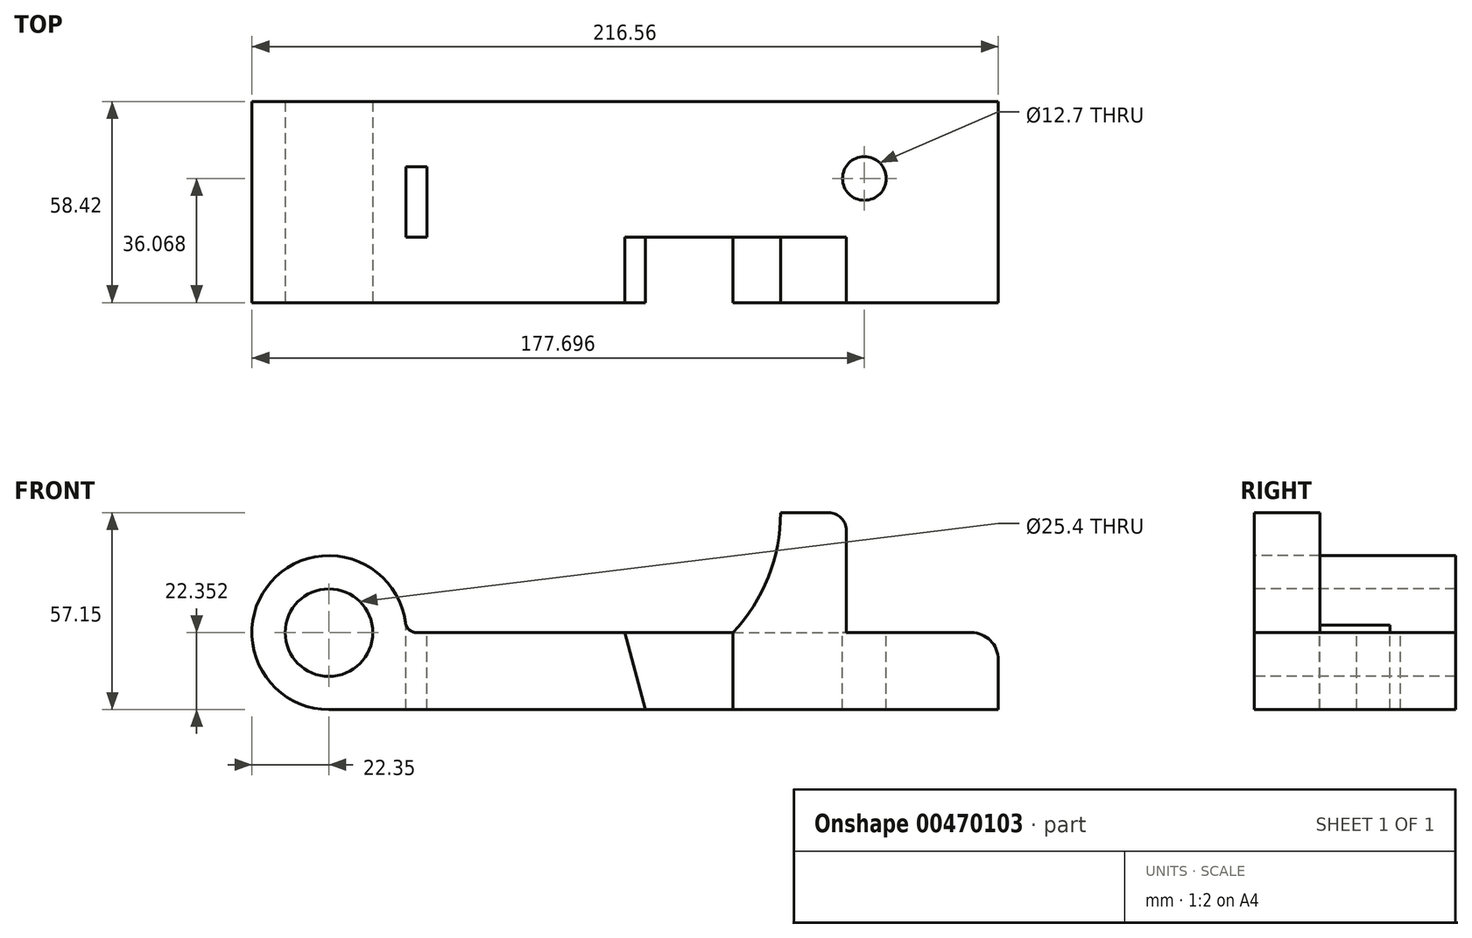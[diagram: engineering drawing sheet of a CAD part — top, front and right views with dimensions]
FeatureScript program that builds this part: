
annotation { "Feature Type Name" : "Feature", "Feature Type Description" : "" }
export const myFeature = defineFeature(function(context is Context, id is Id, definition is map)
    precondition{}
    {
        {
            var Q0;
            Q0=qCreatedBy(makeId("Front.planeOp"),FACE);
            var sketch = newSketch(context, id + "F0", { "sketchPlane" : qUnion([Q0])});
            skLineSegment(sketch, "E0", {"start": v(0, 0) * mm, "end": v(194.2, 0) * mm});
            skCircle(sketch, "E1", {"center": v(0, 22.35) * mm, "radius": 22.35 * mm});
            skPoint(sketch, "E1.second.point", {"position": v(-2.3, 44.58) * mm});
            skPoint(sketch, "E1.third.point", {"position": v(17.77, 35.9) * mm});
            skCircle(sketch, "E2", {"center": v(0, 22.35) * mm, "radius": 12.7 * mm});
            skLineSegment(sketch, "E3", {"start": v(22.35, 22.35) * mm, "end": v(194.2, 22.35) * mm});
            skLineSegment(sketch, "E4", {"start": v(194.2, 22.35) * mm, "end": v(194.2, 0) * mm});
            skLineSegment(sketch, "E5", {"start": v(91.85, 0) * mm, "end": v(85.85, 22.35) * mm});
            skLineSegment(sketch, "E6", {"start": v(117.25, 22.35) * mm, "end": v(117.25, 0) * mm});
            skLineSegment(sketch, "E7", {"start": v(131.04, 57.15) * mm, "end": v(150.09, 57.15) * mm});
            skLineSegment(sketch, "E8", {"start": v(150.09, 57.15) * mm, "end": v(150.09, 22.35) * mm});
            skArc(sketch, "E9", {"start": v(117.25, 22.35) * mm, "mid": v(127.46, 38.43) * mm, "end": v(131.04, 57.15) * mm});
            skPoint(sketch, "E9.third.point", {"position": v(126.77, 36.77) * mm});
            skSolve(sketch);
        }
        {
            var Q0;
            {var subQ0=sQuery(id+"F0.wireOp",EDGE,"E5");Q0=makeQuery(id+"F0.imprint","IMPRINT",FACE,{"disambiguationData":[TD([[makeQuery(id+"F0.imprint","IMPRINT",EDGE,{"derivedFrom":subQ0}),-1.0]])]});}
            var Q1;
            {var subQ3=sQuery(id+"F0.wireOp",EDGE,"E5");Q1=makeQuery(id+"F0.imprint","IMPRINT",FACE,{"disambiguationData":[TD([[makeQuery(id+"F0.imprint","IMPRINT",EDGE,{"derivedFrom":subQ3}),1.0]])]});}
            var Q2;
            {var subQ0=sQuery(id+"F0.wireOp",EDGE,"E4");Q2=makeQuery(id+"F0.imprint","IMPRINT",FACE,{"disambiguationData":[TD([[makeQuery(id+"F0.imprint","IMPRINT",EDGE,{"derivedFrom":subQ0}),-1.0]])]});}
            var Q3;
            Q3=makeQuery(id+"F0.imprint","IMPRINT",FACE,{"disambiguationData":[TD([[makeQuery(id+"F0.imprint","IMPRINT",EDGE,{"derivedFrom":sQuery(id+"F0.wireOp",EDGE,"E2")}),-1.0]])]});
            extrude(context, id + "F1", {"entities" : qUnion([Q0, Q1, Q2, Q3]), "oppositeDirection" : true, "depth" : 58.42 * mm});
        }
        {
            var Q0;
            {var subQ0=sQuery(id+"F0.wireOp",EDGE,"E5");Q0=makeQuery(id+"F0.imprint","IMPRINT",FACE,{"disambiguationData":[TD([[makeQuery(id+"F0.imprint","IMPRINT",EDGE,{"derivedFrom":subQ0}),-1.0]])]});}
            extrude(context, id + "F2", {"entities" : qUnion([Q0]), "operationType" : NewBodyOperationType.REMOVE, "oppositeDirection" : true, "depth" : 19.05 * mm});
        }
        {
            var Q0;
            Q0=makeQuery(id+"F0.imprint","IMPRINT",FACE,{"disambiguationData":[TD([[makeQuery(id+"F0.imprint","IMPRINT",EDGE,{"derivedFrom":sQuery(id+"F0.wireOp",EDGE,"E7")}),-1.0]])]});
            extrude(context, id + "F3", {"entities" : qUnion([Q0]), "operationType" : NewBodyOperationType.ADD, "oppositeDirection" : true, "depth" : 19.05 * mm});
        }
        {
            var Q0;
            Q0=makeQuery(id+"F1.opExtrude","SWEPT_FACE",FACE,{"disambiguationData":[OSD([sQuery(id+"F0.wireOp",EDGE,"E3")])]});
            var sketch = newSketch(context, id + "F4", { "sketchPlane" : qUnion([Q0])});
            skCircle(sketch, "E10", {"center": v(155.35, 36.07) * mm, "radius": 6.35 * mm});
            skLineSegment(sketch, "E11.bottom", {"start": v(-22.35, 19) * mm, "end": v(28.45, 19) * mm});
            skLineSegment(sketch, "E11.top", {"start": v(-22.35, 39.42) * mm, "end": v(28.45, 39.42) * mm});
            skLineSegment(sketch, "E11.left", {"start": v(-22.35, 19) * mm, "end": v(-22.35, 39.42) * mm});
            skLineSegment(sketch, "E11.right", {"start": v(28.45, 19) * mm, "end": v(28.45, 39.42) * mm});
            skLineSegment(sketch, "E12", {"start": v(-22.35, 0) * mm, "end": v(-22.35, 58.42) * mm});
            skSolve(sketch);
        }
        {
            var Q0;
            Q0=makeQuery(id+"F4.imprint","IMPRINT",FACE,{"disambiguationData":[TD([[makeQuery(id+"F4.imprint","IMPRINT",EDGE,{"derivedFrom":sQuery(id+"F4.wireOp",EDGE,"2CULlB4I-Zh7y-c74u-416q-1Dsw6ONQlv81.bottom")}),1.0]])]});
            var Q1;
            Q1=makeQuery(id+"F4.imprint","IMPRINT",FACE,{"disambiguationData":[TD([[makeQuery(id+"F4.imprint","IMPRINT",EDGE,{"derivedFrom":sQuery(id+"F4.wireOp",EDGE,"E10")}),1.0]])]});
            extrude(context, id + "F5", {"entities" : qUnion([Q0, Q1]), "operationType" : NewBodyOperationType.REMOVE, "endBound" : BoundingType.SYMMETRIC, "oppositeDirection" : true, "depth" : 76.2 * mm});
        }
        {
            var Q0;
            Q0=makeQuery(id+"F1.opExtrude","SWEPT_EDGE",EDGE,{"disambiguationData":[OSD([sQuery(id+"F0.wireOp",EDGE,"E1"),sQuery(id+"F0.wireOp",EDGE,"E3")])]});
            var Q1;
            Q1=makeQuery(id+"F3.opExtrude","SWEPT_EDGE",EDGE,{"disambiguationData":[OSD([sQuery(id+"F0.wireOp",EDGE,"E3"),sQuery(id+"F0.wireOp",EDGE,"E8")])]});
            fillet(context, id + "F6", {"entities" : qUnion([Q0, Q1]), "radius" : 3.3 * mm, "tangentPropagation" : true, "allowEdgeOverflow" : false});
        }
        {
            var Q0;
            Q0=makeQuery(id+"F3.opExtrude","SWEPT_EDGE",EDGE,{"disambiguationData":[OSD([sQuery(id+"F0.wireOp",EDGE,"E7"),sQuery(id+"F0.wireOp",EDGE,"E8")])]});
            fillet(context, id + "F7", {"entities" : qUnion([Q0]), "radius" : 5.08 * mm, "tangentPropagation" : true, "allowEdgeOverflow" : false});
        }
        {
            var Q0;
            Q0=makeQuery(id+"F1.opExtrude","SWEPT_EDGE",EDGE,{"disambiguationData":[OSD([sQuery(id+"F0.wireOp",EDGE,"E3"),sQuery(id+"F0.wireOp",EDGE,"E4")])]});
            fillet(context, id + "F8", {"entities" : qUnion([Q0]), "radius" : 7.87 * mm, "tangentPropagation" : true, "allowEdgeOverflow" : false});
        }
        {
            var Q0;
            {var subQ0=sQuery(id+"F4.wireOp",EDGE,"E12");var subQ1=sQuery(id+"F4.wireOp",EDGE,"E11.bottom");var subQ2=makeQuery(id+"F4.imprint","INTERSECT",VERTEX,{"derivedFrom":[subQ1,subQ0]});Q0=makeQuery(id+"F4.imprint","IMPRINT",FACE,{"disambiguationData":[TD([[makeQuery(id+"F4.imprint","IMPRINT",EDGE,{"disambiguationData":[TD([[subQ2,-1.0]])],"derivedFrom":subQ0}),-1.0]])]});}
            var Q1;
            {var subQ0=sQuery(id+"F4.wireOp",EDGE,"E11.right");Q1=makeQuery(id+"F4.imprint","IMPRINT",FACE,{"disambiguationData":[TD([[makeQuery(id+"F4.imprint","IMPRINT",EDGE,{"derivedFrom":subQ0}),1.0]])]});}
            var Q2;
            Q2=makeQuery(id+"F4.imprint","IMPRINT",FACE,{"disambiguationData":[TD([[makeQuery(id+"F4.imprint","IMPRINT",EDGE,{"derivedFrom":sQuery(id+"F4.wireOp",EDGE,"E10")}),1.0]])]});
            extrude(context, id + "F9", {"entities" : qUnion([Q0, Q1, Q2]), "operationType" : NewBodyOperationType.REMOVE, "endBound" : BoundingType.SYMMETRIC, "oppositeDirection" : true, "depth" : 76.2 * mm});
        }
    });
